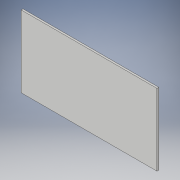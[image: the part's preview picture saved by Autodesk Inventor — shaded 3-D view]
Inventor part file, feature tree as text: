
AUTODESK INVENTOR PART (.ipt)
format: ipt  version: 2017 (Build 210142000, 142)  size: 85,504 bytes
history: native  units: in
note: dims shown in document units (in); Inventor stores cm internally (conversion verified against a paired STEP export)
features: extrude x1, sketch x1
ambient origin geometry x8: Origin, YZ Plane, XZ Plane, XY Plane, X Axis, Y Axis, Z Axis, Center Point
bodies: Solid1 (feature_tree)
feature tree (2):
  extrude  "Extrusion1"  Depth=19.0in
  sketch  "Sketch1"  dims[d0=36.0in d1=19.0in d2=0.5in d3=0.0in]
